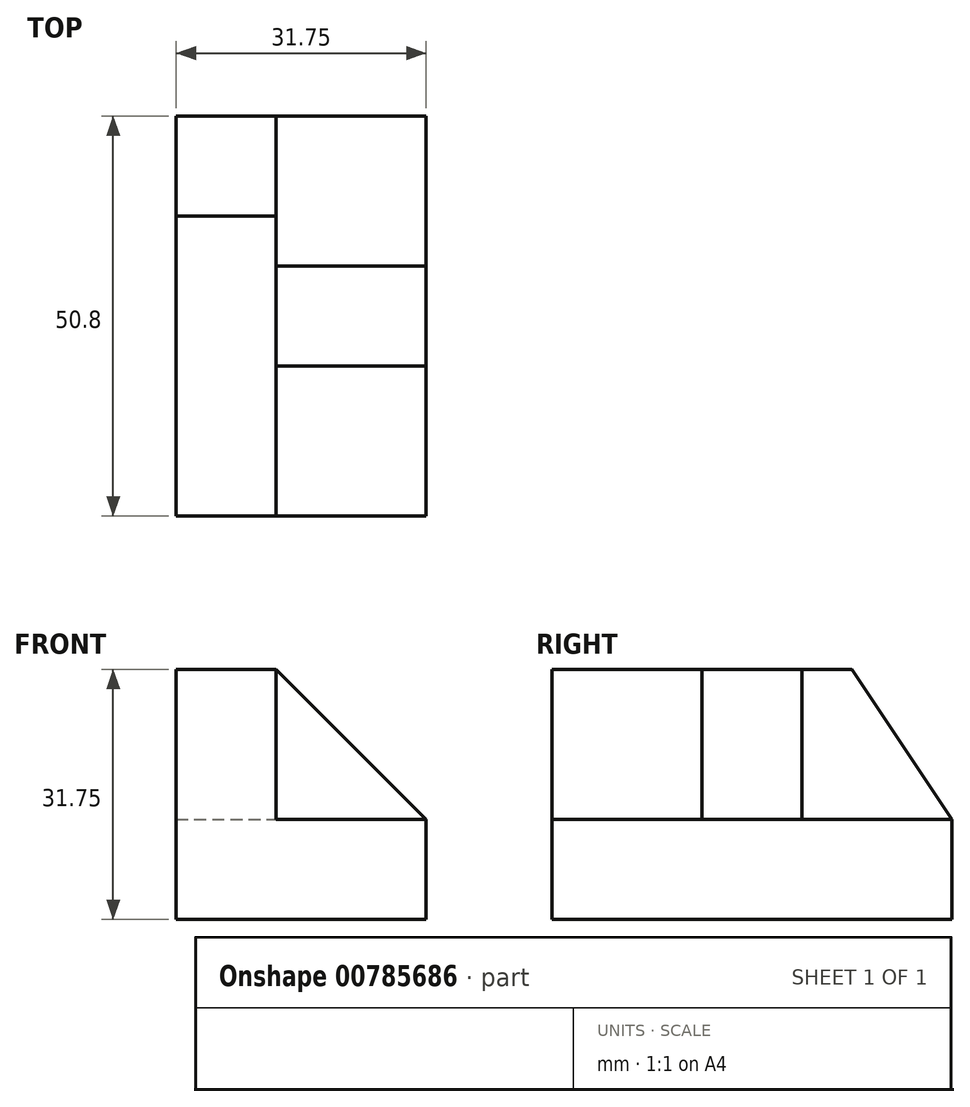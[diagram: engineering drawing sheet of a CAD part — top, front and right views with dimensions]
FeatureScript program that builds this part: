
annotation { "Feature Type Name" : "Feature", "Feature Type Description" : "" }
export const myFeature = defineFeature(function(context is Context, id is Id, definition is map)
    precondition{}
    {
        {
            var Q0;
            Q0=qCreatedBy(makeId("Front.planeOp"),FACE);
            var sketch = newSketch(context, id + "F0", { "sketchPlane" : qUnion([Q0])});
            skLineSegment(sketch, "E0", {"start": v(0, 0) * mm, "end": v(31.75, 0) * mm});
            skLineSegment(sketch, "E1", {"start": v(31.75, 0) * mm, "end": v(31.75, 31.75) * mm});
            skLineSegment(sketch, "E2", {"start": v(31.75, 31.75) * mm, "end": v(0, 31.75) * mm});
            skLineSegment(sketch, "E3", {"start": v(0, 31.75) * mm, "end": v(0, 0) * mm});
            skSolve(sketch);
        }
        {
            var Q0;
            Q0=makeQuery(id+"F0.imprint","IMPRINT",FACE,{"disambiguationData":[TD([[makeQuery(id+"F0.imprint","IMPRINT",EDGE,{"derivedFrom":sQuery(id+"F0.wireOp",EDGE,"E0")}),1.0]])]});
            extrude(context, id + "F1", {"entities" : qUnion([Q0]), "depth" : 50.8 * mm, "offsetDistance" : 25.4 * mm});
        }
        {
            var Q0;
            Q0=makeQuery(id+"F1.opExtrude","SWEPT_FACE",FACE,{"disambiguationData":[OSD([sQuery(id+"F0.wireOp",EDGE,"E1")])]});
            var sketch = newSketch(context, id + "F2", { "sketchPlane" : qUnion([Q0])});
            skLineSegment(sketch, "E4", {"start": v(0, 0) * mm, "end": v(0, 12.7) * mm});
            skLineSegment(sketch, "E5", {"start": v(0, 12.7) * mm, "end": v(-19.05, 12.7) * mm});
            skLineSegment(sketch, "E6", {"start": v(-19.05, 12.7) * mm, "end": v(-19.05, 31.75) * mm});
            skSolve(sketch);
        }
        {
            var Q0;
            {var subQ0=sQuery(id+"F2.wireOp",EDGE,"E5");Q0=makeQuery(id+"F2.imprint","IMPRINT",FACE,{"disambiguationData":[TD([[makeQuery(id+"F2.imprint","IMPRINT",EDGE,{"derivedFrom":subQ0}),-1.0]])]});}
            extrude(context, id + "F3", {"entities" : qUnion([Q0]), "operationType" : NewBodyOperationType.REMOVE, "oppositeDirection" : true, "depth" : 19.05 * mm, "offsetDistance" : 25.4 * mm});
        }
        {
            var Q0;
            Q0=makeQuery(id+"F1.opExtrude","SWEPT_FACE",FACE,{"disambiguationData":[OSD([sQuery(id+"F0.wireOp",EDGE,"E1")])]});
            var sketch = newSketch(context, id + "F4", { "sketchPlane" : qUnion([Q0])});
            skLineSegment(sketch, "E7", {"start": v(-50.8, 0) * mm, "end": v(-50.8, 12.7) * mm});
            skLineSegment(sketch, "E8", {"start": v(-50.8, 12.7) * mm, "end": v(-31.75, 12.7) * mm});
            skLineSegment(sketch, "E9", {"start": v(-31.75, 12.7) * mm, "end": v(-31.75, 31.75) * mm});
            skSolve(sketch);
        }
        {
            var Q0;
            {var subQ0=sQuery(id+"F4.wireOp",EDGE,"E8");Q0=makeQuery(id+"F4.imprint","IMPRINT",FACE,{"disambiguationData":[TD([[makeQuery(id+"F4.imprint","IMPRINT",EDGE,{"derivedFrom":subQ0}),1.0]])]});}
            extrude(context, id + "F5", {"entities" : qUnion([Q0]), "operationType" : NewBodyOperationType.REMOVE, "oppositeDirection" : true, "depth" : 19.05 * mm, "offsetDistance" : 25.4 * mm});
        }
        {
            var Q0;
            Q0=makeQuery(id+"F3.boolean.opBoolean","COPY",FACE,{"derivedFrom":makeQuery(id+"F3.opExtrude","SWEPT_FACE",FACE,{"disambiguationData":[OSD([sQuery(id+"F2.wireOp",EDGE,"E6")])]})});
            var sketch = newSketch(context, id + "F6", { "sketchPlane" : qUnion([Q0])});
            skLineSegment(sketch, "E10", {"start": v(-31.75, 12.7) * mm, "end": v(-12.7, 31.75) * mm});
            skSolve(sketch);
        }
        {
            var Q0;
            Q0=makeQuery(id+"F6.imprint","IMPRINT",FACE,{"disambiguationData":[TD([[makeQuery(id+"F6.imprint","IMPRINT",EDGE,{"derivedFrom":sQuery(id+"F6.wireOp",EDGE,"E10")}),1.0]])]});
            extrude(context, id + "F7", {"entities" : qUnion([Q0]), "operationType" : NewBodyOperationType.REMOVE, "oppositeDirection" : true, "depth" : 25.4 * mm, "offsetDistance" : 25.4 * mm});
        }
        {
            var Q0;
            Q0=makeQuery(id+"F3.boolean.opBoolean","COPY",FACE,{"derivedFrom":makeQuery(id+"F3.opExtrude","CAP_FACE",FACE,{"disambiguationData":[OSD([sQuery(id+"F0.wireOp",EDGE,"E1"),sQuery(id+"F0.wireOp",EDGE,"E2"),sQuery(id+"F2.wireOp",EDGE,"E5"),sQuery(id+"F2.wireOp",EDGE,"E6")])],"isStart":false})});
            var sketch = newSketch(context, id + "F8", { "sketchPlane" : qUnion([Q0])});
            skLineSegment(sketch, "E11", {"start": v(-19.05, 31.75) * mm, "end": v(-12.7, 31.75) * mm});
            skLineSegment(sketch, "E12", {"start": v(-12.7, 31.75) * mm, "end": v(0, 12.7) * mm});
            skSolve(sketch);
        }
        {
            var Q0;
            {var subQ0=sQuery(id+"F8.wireOp",EDGE,"E12");Q0=makeQuery(id+"F8.imprint","IMPRINT",FACE,{"disambiguationData":[TD([[makeQuery(id+"F8.imprint","IMPRINT",EDGE,{"derivedFrom":subQ0}),1.0]])]});}
            extrude(context, id + "F9", {"entities" : qUnion([Q0]), "operationType" : NewBodyOperationType.REMOVE, "oppositeDirection" : true, "depth" : 25.4 * mm, "offsetDistance" : 25.4 * mm});
        }
    });
